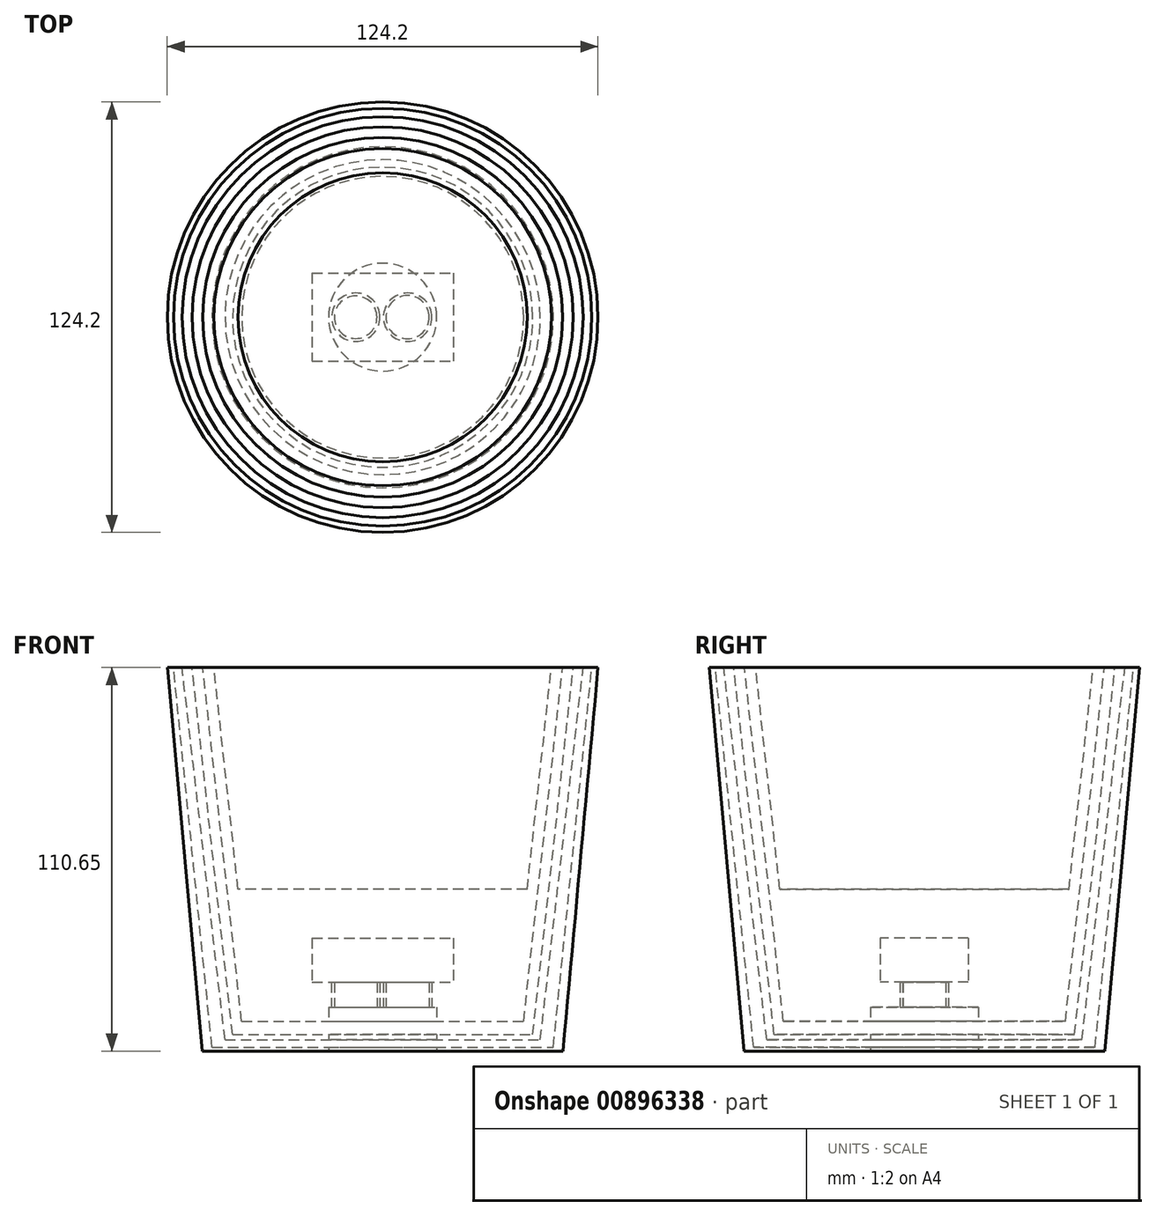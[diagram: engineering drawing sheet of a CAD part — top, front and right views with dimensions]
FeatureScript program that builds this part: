
annotation { "Feature Type Name" : "Feature", "Feature Type Description" : "" }
export const myFeature = defineFeature(function(context is Context, id is Id, definition is map)
    precondition{}
    {
        {
            var Q0;
            Q0=qCreatedBy(makeId("Front.planeOp"),FACE);
            var sketch = newSketch(context, id + "F0", { "sketchPlane" : qUnion([Q0])});
            skLineSegment(sketch, "E0", {"start": v(-51.98, -46.63) * mm, "end": v(-62.1, 64.02) * mm});
            skLineSegment(sketch, "E1", {"start": v(-62.1, 64.02) * mm, "end": v(0, 64.02) * mm});
            skLineSegment(sketch, "E2", {"start": v(0, 64.02) * mm, "end": v(0, -46.63) * mm});
            skLineSegment(sketch, "E3", {"start": v(0, -46.63) * mm, "end": v(-51.98, -46.63) * mm});
            skSolve(sketch);
        }
        {
            var Q0;
            Q0 = qSketchRegion(id + "F0", true);
            var Q1;
            Q1=sQuery(id+"F0.wireOp",EDGE,"E2");
            revolve(context, id + "F1", {"surfaceOperationType" : NewSurfaceOperationType.NEW, "entities" : qUnion([Q0]), "axis" : qUnion([Q1]), "revolveType" : RevolveType.FULL});
        }
        {
            var Q0;
            Q0=makeQuery(id+"F1.opRevolve","SWEPT_FACE",FACE,{"disambiguationData":[OSD([sQuery(id+"F0.wireOp",EDGE,"E3")])]});
            cPlane(context, id + "F2", {"entities" : qUnion([Q0]), "cplaneType" : CPlaneType.OFFSET, "offset" : 0 * mm, "width" : 152.4 * mm, "height" : 152.4 * mm});
        }
        {
            var Q0;
            Q0=qCreatedBy(id+"F2.planeOp",FACE);
            var sketch = newSketch(context, id + "F3", { "sketchPlane" : qUnion([Q0])});
            skCircle(sketch, "E4", {"center": v(0, 0) * mm, "radius": 15.58 * mm});
            skSolve(sketch);
        }
        {
            var Q0;
            Q0=makeQuery(id+"F3.imprint","IMPRINT",FACE,{"disambiguationData":[TD([[makeQuery(id+"F3.imprint","IMPRINT",EDGE,{"derivedFrom":sQuery(id+"F3.wireOp",EDGE,"E4")}),1.0]])]});
            extrude(context, id + "F4", {"entities" : qUnion([Q0]), "operationType" : NewBodyOperationType.REMOVE, "oppositeDirection" : true, "depth" : 12.7 * mm, "offsetDistance" : 25.4 * mm});
        }
        {
            var Q0;
            Q0=qCreatedBy(makeId("Front.planeOp"),FACE);
            var sketch = newSketch(context, id + "F5", { "sketchPlane" : qUnion([Q0])});
            skLineSegment(sketch, "E5.bottom", {"start": v(-20.32, -14.04) * mm, "end": v(20.32, -14.04) * mm});
            skLineSegment(sketch, "E5.top", {"start": v(-20.32, -26.74) * mm, "end": v(20.32, -26.74) * mm});
            skLineSegment(sketch, "E5.left", {"start": v(-20.32, -14.04) * mm, "end": v(-20.32, -26.74) * mm});
            skLineSegment(sketch, "E5.right", {"start": v(20.32, -14.04) * mm, "end": v(20.32, -26.74) * mm});
            skSolve(sketch);
        }
        {
            var Q0;
            Q0 = qSketchRegion(id + "F5", true);
            extrude(context, id + "F6", {"entities" : qUnion([Q0]), "operationType" : NewBodyOperationType.REMOVE, "endBound" : BoundingType.SYMMETRIC, "oppositeDirection" : true, "depth" : 25.4 * mm, "offsetDistance" : 25.4 * mm});
        }
        {
            var Q0;
            Q0=qCreatedBy(makeId("Front.planeOp"),FACE);
            var sketch = newSketch(context, id + "F7", { "sketchPlane" : qUnion([Q0])});
            skLineSegment(sketch, "E6", {"start": v(0, 68.78) * mm, "end": v(49.17, 68.78) * mm});
            skLineSegment(sketch, "E7", {"start": v(49.17, 68.78) * mm, "end": v(41.68, 0) * mm});
            skLineSegment(sketch, "E8", {"start": v(41.68, 0) * mm, "end": v(0, 0) * mm});
            skLineSegment(sketch, "E9", {"start": v(0, 0) * mm, "end": v(0, 68.78) * mm});
            skSolve(sketch);
        }
        {
            var Q0;
            Q0 = qSketchRegion(id + "F7", true);
            var Q1;
            Q1=sQuery(id+"F7.wireOp",EDGE,"E9");
            revolve(context, id + "F8", {"operationType" : NewBodyOperationType.REMOVE, "surfaceOperationType" : NewSurfaceOperationType.NEW, "entities" : qUnion([Q0]), "axis" : qUnion([Q1]), "revolveType" : RevolveType.FULL, "oppositeDirection" : true});
        }
        {
            var Q0;
            Q0=qCreatedBy(makeId("Front.planeOp"),FACE);
            var sketch = newSketch(context, id + "F9", { "sketchPlane" : qUnion([Q0])});
            skLineSegment(sketch, "E10", {"start": v(15.36, -38.07) * mm, "end": v(40.65, -38.07) * mm});
            skLineSegment(sketch, "E11", {"start": v(40.65, -38.07) * mm, "end": v(52, 65.17) * mm});
            skLineSegment(sketch, "E12", {"start": v(52, 65.17) * mm, "end": v(55.04, 64.84) * mm});
            skLineSegment(sketch, "E13", {"start": v(55.04, 64.84) * mm, "end": v(43.3, -41.86) * mm});
            skLineSegment(sketch, "E14", {"start": v(43.3, -41.86) * mm, "end": v(15.36, -41.86) * mm});
            skLineSegment(sketch, "E15", {"start": v(15.36, -41.86) * mm, "end": v(0, -41.86) * mm});
            skLineSegment(sketch, "E16", {"start": v(0, -41.86) * mm, "end": v(0, -38.07) * mm});
            skLineSegment(sketch, "E17", {"start": v(0, -38.07) * mm, "end": v(15.36, -38.07) * mm});
            skSolve(sketch);
        }
        {
            var Q0;
            Q0 = qSketchRegion(id + "F9", true);
            var Q1;
            Q1=sQuery(id+"F9.wireOp",EDGE,"E16");
            revolve(context, id + "F10", {"operationType" : NewBodyOperationType.REMOVE, "surfaceOperationType" : NewSurfaceOperationType.NEW, "entities" : qUnion([Q0]), "axis" : qUnion([Q1]), "revolveType" : RevolveType.FULL});
        }
        {
            var Q0;
            Q0=makeQuery(id+"F4.boolean.opBoolean","COPY",FACE,{"derivedFrom":makeQuery(id+"F4.opExtrude","CAP_FACE",FACE,{"disambiguationData":[OSD([sQuery(id+"F3.wireOp",EDGE,"E4")])],"isStart":false})});
            var sketch = newSketch(context, id + "F11", { "sketchPlane" : qUnion([Q0])});
            skCircle(sketch, "E18", {"center": v(-7.76, 0) * mm, "radius": 6.98 * mm});
            skCircle(sketch, "E19", {"center": v(7.2, 0) * mm, "radius": 6.98 * mm});
            skCircle(sketch, "E20", {"center": v(-7.76, 0) * mm, "radius": 6.13 * mm});
            skCircle(sketch, "E21", {"center": v(7.2, 0) * mm, "radius": 6.23 * mm});
            skSolve(sketch);
        }
        {
            var Q0;
            Q0 = qSketchRegion(id + "F11", true);
            extrude(context, id + "F12", {"entities" : qUnion([Q0]), "operationType" : NewBodyOperationType.REMOVE, "oppositeDirection" : true, "depth" : 12.7 * mm, "offsetDistance" : 25.4 * mm});
        }
        {
            var Q0;
            Q0=qCreatedBy(makeId("Front.planeOp"),FACE);
            var sketch = newSketch(context, id + "F13", { "sketchPlane" : qUnion([Q0])});
            skLineSegment(sketch, "E22", {"start": v(57.9, 64.66) * mm, "end": v(45.45, -43.4) * mm});
            skLineSegment(sketch, "E23", {"start": v(45.45, -43.4) * mm, "end": v(0, -43.4) * mm});
            skLineSegment(sketch, "E24", {"start": v(0, -43.4) * mm, "end": v(0, -45.5) * mm});
            skLineSegment(sketch, "E25", {"start": v(0, -45.5) * mm, "end": v(49.22, -45.5) * mm});
            skLineSegment(sketch, "E26", {"start": v(49.22, -45.5) * mm, "end": v(60.37, 64.89) * mm});
            skLineSegment(sketch, "E27", {"start": v(60.37, 64.89) * mm, "end": v(57.9, 64.66) * mm});
            skSolve(sketch);
        }
        {
            var Q0;
            Q0 = qSketchRegion(id + "F13", true);
            var Q1;
            Q1=sQuery(id+"F13.wireOp",EDGE,"E24");
            revolve(context, id + "F14", {"operationType" : NewBodyOperationType.REMOVE, "surfaceOperationType" : NewSurfaceOperationType.NEW, "entities" : qUnion([Q0]), "axis" : qUnion([Q1]), "revolveType" : RevolveType.FULL, "oppositeDirection" : true});
        }
    });
